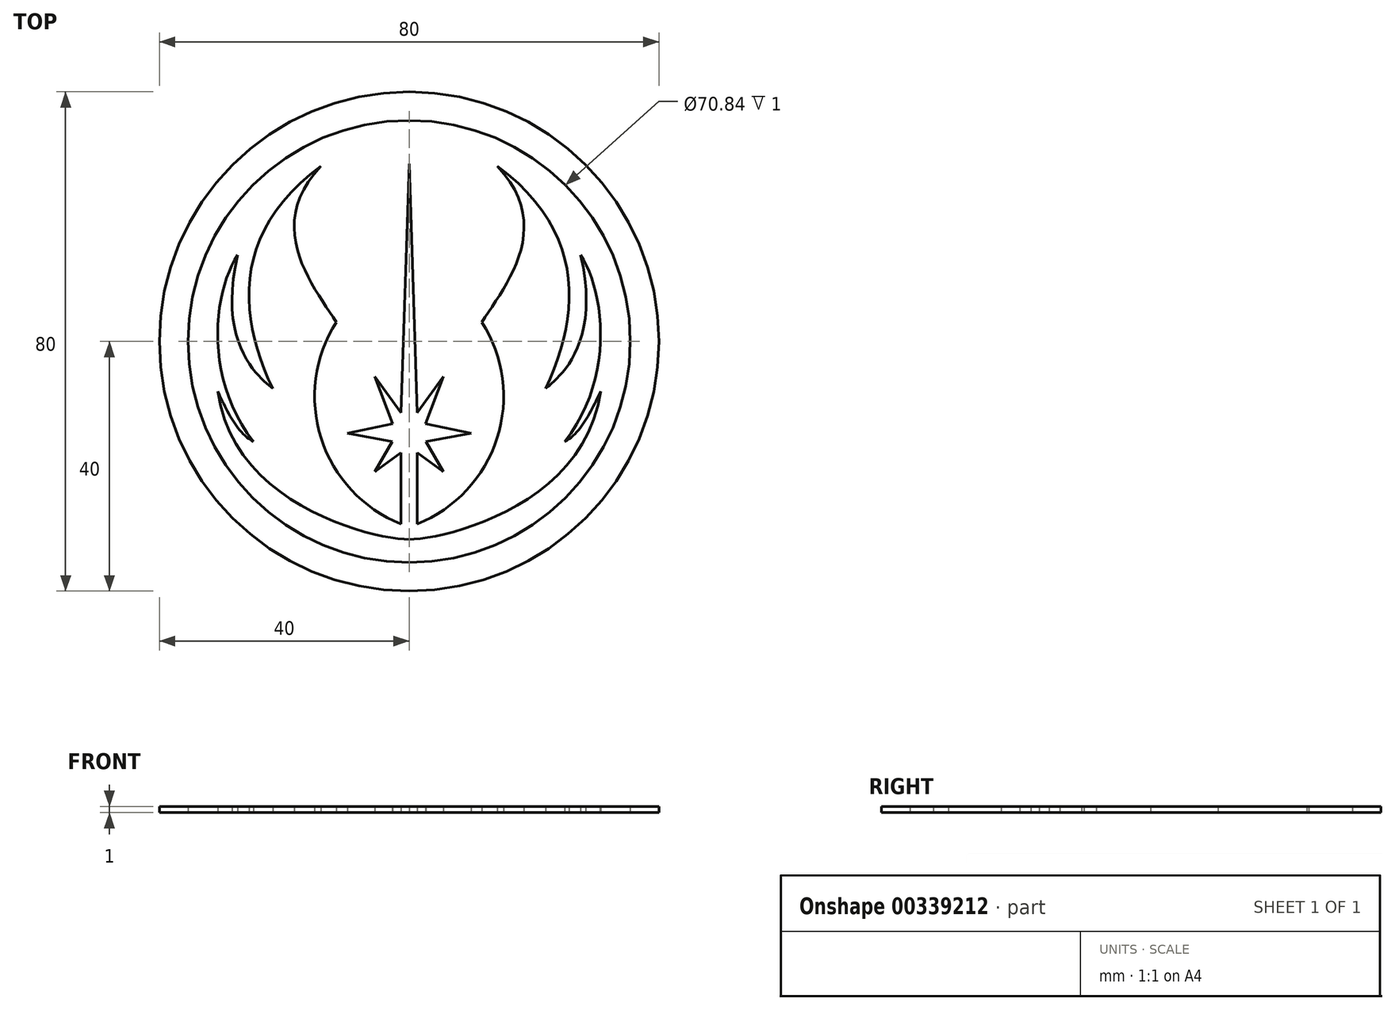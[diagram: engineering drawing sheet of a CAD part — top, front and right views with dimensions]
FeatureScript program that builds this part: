
annotation { "Feature Type Name" : "Feature", "Feature Type Description" : "" }
export const myFeature = defineFeature(function(context is Context, id is Id, definition is map)
    precondition{}
    {
        {
            var Q0;
            Q0=qCreatedBy(makeId("Top.planeOp"),FACE);
            var sketch = newSketch(context, id + "F0", { "sketchPlane" : qUnion([Q0])});
            skCircle(sketch, "E0", {"center": v(0, 0) * mm, "radius": 40 * mm});
            skPoint(sketch, "E0.centerSnap0", {"position": v(0, 44.26) * mm});
            skPoint(sketch, "E0.centerSnap1", {"position": v(-44.26, 0) * mm});
            skCircle(sketch, "E1", {"center": v(0, 0) * mm, "radius": 35.42 * mm});
            skLineSegment(sketch, "E2", {"start": v(0, 28.48) * mm, "end": v(-1.31, -11.41) * mm});
            skLineSegment(sketch, "E3", {"start": v(-1.31, -11.41) * mm, "end": v(-5.5, -5.62) * mm});
            skLineSegment(sketch, "E4", {"start": v(-5.5, -5.62) * mm, "end": v(-2.65, -13.16) * mm});
            skLineSegment(sketch, "E5", {"start": v(-2.65, -13.16) * mm, "end": v(-9.9, -14.73) * mm});
            skLineSegment(sketch, "E6", {"start": v(-9.9, -14.73) * mm, "end": v(-2.7, -16.06) * mm});
            skLineSegment(sketch, "E7", {"start": v(-2.7, -16.06) * mm, "end": v(-5.5, -20.85) * mm});
            skLineSegment(sketch, "E8", {"start": v(-5.5, -20.85) * mm, "end": v(-1.31, -17.81) * mm});
            skLineSegment(sketch, "E9", {"start": v(-1.31, -17.81) * mm, "end": v(-1.31, -29.24) * mm});
            skArc(sketch, "E10", {"start": v(-11.67, 3.1) * mm, "mid": v(-14.09, -15.5) * mm, "end": v(-1.31, -29.24) * mm});
            skFitSpline(sketch, "E11", {"points": [v(-11.67, 3.1) * mm, v(-14.1, 28.12) * mm], "startDerivative": vector(-11.1, 17.77) * mm, "endDerivative": vector(27.75, 29.38) * mm});
            skFitSpline(sketch, "E12", {"points": [v(-14.1, 28.12) * mm, v(-21.84, -7.55) * mm], "startDerivative": vector(-42.44, -31.2) * mm, "endDerivative": vector(17.05, -35.55) * mm});
            skFitSpline(sketch, "E13", {"points": [v(-21.84, -7.55) * mm, v(-27.46, 13.88) * mm], "startDerivative": vector(-2.16, 2.43) * mm, "endDerivative": vector(11.06, 46.8) * mm});
            skFitSpline(sketch, "E14", {"points": [v(-27.46, 13.88) * mm, v(-24.92, -16.05) * mm], "startDerivative": vector(-11.43, -17.6) * mm, "endDerivative": vector(24.3, -31.2) * mm});
            skFitSpline(sketch, "E15", {"points": [v(-24.92, -16.05) * mm, v(-30.67, -7.95) * mm], "startDerivative": vector(-8.16, 4.35) * mm, "endDerivative": vector(-4.17, 8.89) * mm});
            skFitSpline(sketch, "E16", {"points": [v(-30.67, -7.95) * mm, v(0, -31.71) * mm], "startDerivative": vector(7.44, -55.5) * mm, "endDerivative": vector(16.36, 0) * mm});
            skLineSegment(sketch, "E17.MirrorCS", {"start": v(5.5, -20.85) * mm, "end": v(1.31, -17.81) * mm});
            skFitSpline(sketch, "E18.MirrorCS", {"points": [v(24.92, -16.05) * mm, v(30.67, -7.95) * mm], "startDerivative": vector(8.16, 4.35) * mm, "endDerivative": vector(4.17, 8.89) * mm});
            skFitSpline(sketch, "E19.MirrorCS", {"points": [v(27.46, 13.88) * mm, v(24.92, -16.05) * mm], "startDerivative": vector(11.43, -17.6) * mm, "endDerivative": vector(-24.3, -31.2) * mm});
            skLineSegment(sketch, "E20.MirrorCS", {"start": v(2.7, -16.06) * mm, "end": v(5.5, -20.85) * mm});
            skLineSegment(sketch, "E21.MirrorCS", {"start": v(2.65, -13.16) * mm, "end": v(9.9, -14.73) * mm});
            skFitSpline(sketch, "E22.MirrorCS", {"points": [v(21.84, -7.55) * mm, v(27.46, 13.88) * mm], "startDerivative": vector(2.16, 2.43) * mm, "endDerivative": vector(-11.06, 46.8) * mm});
            skArc(sketch, "E23.MirrorCS", {"start": v(11.67, 3.1) * mm, "mid": v(14.09, -15.5) * mm, "end": v(1.31, -29.24) * mm});
            skFitSpline(sketch, "E24.MirrorCS", {"points": [v(11.67, 3.1) * mm, v(14.1, 28.12) * mm], "startDerivative": vector(11.1, 17.77) * mm, "endDerivative": vector(-27.75, 29.38) * mm});
            skLineSegment(sketch, "E25.MirrorCS", {"start": v(1.31, -11.41) * mm, "end": v(5.5, -5.62) * mm});
            skFitSpline(sketch, "E26.MirrorCS", {"points": [v(30.67, -7.95) * mm, v(0, -31.71) * mm], "startDerivative": vector(-7.44, -55.5) * mm, "endDerivative": vector(-16.36, 0) * mm});
            skLineSegment(sketch, "E27.MirrorCS", {"start": v(5.5, -5.62) * mm, "end": v(2.65, -13.16) * mm});
            skFitSpline(sketch, "E28.MirrorCS", {"points": [v(14.1, 28.12) * mm, v(21.84, -7.55) * mm], "startDerivative": vector(42.44, -31.2) * mm, "endDerivative": vector(-17.05, -35.55) * mm});
            skLineSegment(sketch, "E29.MirrorCS", {"start": v(9.9, -14.73) * mm, "end": v(2.7, -16.06) * mm});
            skLineSegment(sketch, "E30.MirrorCS", {"start": v(0, 28.48) * mm, "end": v(1.31, -11.41) * mm});
            skLineSegment(sketch, "E31.MirrorCS", {"start": v(1.31, -17.81) * mm, "end": v(1.31, -29.24) * mm});
            skSolve(sketch);
        }
        {
            var Q0;
            Q0=makeQuery(id+"F0.imprint","IMPRINT",FACE,{"disambiguationData":[TD([[makeQuery(id+"F0.imprint","IMPRINT",EDGE,{"derivedFrom":sQuery(id+"F0.wireOp",EDGE,"E1")}),-1.0]])]});
            var Q1;
            Q1=makeQuery(id+"F0.imprint","IMPRINT",FACE,{"disambiguationData":[TD([[makeQuery(id+"F0.imprint","IMPRINT",EDGE,{"derivedFrom":sQuery(id+"F0.wireOp",EDGE,"E2")}),1.0]])]});
            extrude(context, id + "F1", {"entities" : qUnion([Q0, Q1]), "depth" : 1 * mm});
        }
    });
